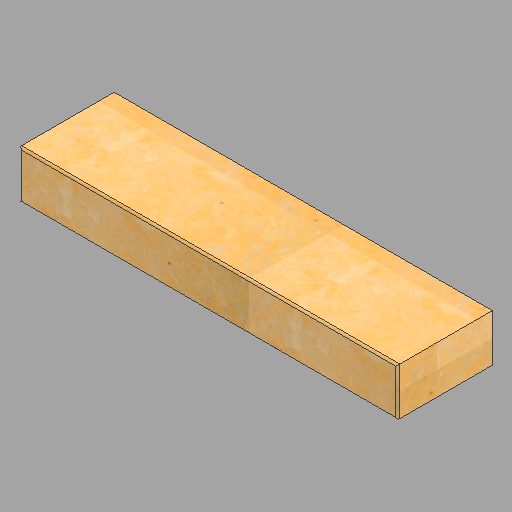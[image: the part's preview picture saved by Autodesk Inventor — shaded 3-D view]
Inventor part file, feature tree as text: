
AUTODESK INVENTOR PART (.ipt)
format: ipt  version: 2023 (Build 270158030, 158C)  size: 252,416 bytes
history: native  units: in
note: dims shown in document units (in); Inventor stores cm internally (conversion verified against a paired STEP export)
features: fillet x2, extrude x1, direct_edit x1, sketch x1, move_body x1
ambient origin geometry x8: Origin, YZ Plane, XZ Plane, XY Plane, X Axis, Y Axis, Z Axis, Center Point
bodies: Solid1 (feature_tree)
feature tree (6):
  extrude  "Extrusion1"  Depth=0.125in
  fillet  "Fillet1"  Radius=48.0in
  fillet  "Fillet2"  Radius=0.25in
  direct_edit  "Direct Edit1"
  sketch  "Sketch1"  dims[d0=6.0in d1=10.0in d2=48.0in d3=0.0in d4=0.25in d5=0.125in d6=0.0in d7=0.0in d8=2.0in]
  move_body  "Move1"
